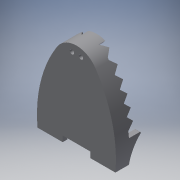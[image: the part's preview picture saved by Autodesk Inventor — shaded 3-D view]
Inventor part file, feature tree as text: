
AUTODESK INVENTOR PART (.ipt)
format: ipt  version: 2016 (Build 200138000, 138)  size: 520,192 bytes
history: native  units: in
note: dims shown in document units (in); Inventor stores cm internally (conversion verified against a paired STEP export)
features: sketch x27, extrude x26, other x12, plane x12, projected_geometry x8, reference x2, fillet x1
ambient origin geometry x8: Origin, YZ Plane, XZ Plane, XY Plane, X Axis, Y Axis, Z Axis, Center Point
bodies: Solid1 (feature_tree)
feature tree (88):
  extrude  "Extrusion1"  Depth=1.0in
  extrude  "Extrusion2"  Depth=0.3937in TaperAngle=0.0deg
  extrude  "Extrusion3"  Depth=1.0in
  extrude  "Extrusion4"  Depth=1.0in TaperAngle=0.0deg
  sketch  "Sketch5"  dims[d12=1.0in d13=0.0in d15=0.5in]
  other  "Work Point1"
  other  "Work Point2"
  other  "Work Point3"
  other  "Work Point4"
  other  "Work Point5"
  other  "Work Point6"
  other  "Work Point7"
  other  "Work Point8"
  other  "Work Point9"
  other  "Work Point10"
  other  "Work Point11"
  other  "Work Point12"
  plane  "Work Plane1"
  plane  "Work Plane2"
  plane  "Work Plane3"
  plane  "Work Plane4"
  plane  "Work Plane5"
  plane  "Work Plane6"
  sketch  "Sketch6"  dims[d16=2.3622in d18=0.45in d19=0.3937in d21=1.0in d23=0.25in]
  sketch  "Sketch7"  dims[d24=0.5in d25=0.25in]
  sketch  "Sketch8"  dims[d26=0.25in d27=0.5in d28=0.25in d29=0.25in d30=0.5in d31=0.25in]
  sketch  "Sketch9"  dims[d32=0.25in d33=0.5in d34=0.25in d35=0.25in d36=0.5in d37=0.25in]
  sketch  "Sketch10"  dims[d38=0.25in d39=0.5in d40=0.25in d44=1.0in d45=0.0in]
  sketch  "Sketch11"  dims[d46=1.0in d47=0.0in d48=1.0in d49=0.0in]
  extrude  "Extrusion5"  Depth=0.5in
  extrude  "Extrusion6"  Depth=0.3937in
  extrude  "Extrusion7"  Depth=0.25in
  extrude  "Extrusion8"  Depth=0.25in
  extrude  "Extrusion9"  Depth=0.25in
  extrude  "Extrusion10"  Depth=1.0in TaperAngle=0.0deg
  plane  "Work Plane7"
  plane  "Work Plane8"
  plane  "Work Plane9"
  plane  "Work Plane10"
  plane  "Work Plane11"
  plane  "Work Plane12"
  sketch  "Sketch13"  dims[d50=1.0in d51=0.0in d52=1.0in d53=0.0in]
  sketch  "Sketch14"  dims[d54=1.0in d55=0.0in d56=0.25in]
  sketch  "Sketch15"  dims[d57=0.5in d58=0.25in]
  sketch  "Sketch16"  dims[d59=0.25in d60=0.5in d61=0.25in d62=0.25in d63=0.5in d64=0.25in]
  sketch  "Sketch17"  dims[d65=0.25in d66=0.5in d67=0.25in d68=0.25in d69=0.5in d70=0.25in]
  sketch  "Sketch18"  dims[d71=0.25in d72=0.5in d73=0.25in d74=1.0in d75=0.0in]
  extrude  "Extrusion11"  Depth=1.0in TaperAngle=0.0deg
  extrude  "Extrusion12"  Depth=1.0in TaperAngle=0.0deg
  extrude  "Extrusion13"  Depth=0.25in
  extrude  "Extrusion14"  Depth=0.25in
  extrude  "Extrusion15"  Depth=0.25in
  extrude  "Extrusion16"  Depth=0.25in
  extrude  "Extrusion17"  Depth=1.0in TaperAngle=0.0deg
  extrude  "Extrusion18"  Depth=1.0in TaperAngle=0.0deg
  extrude  "Extrusion19"  Depth=1.0in TaperAngle=0.0deg
  extrude  "Extrusion20"  Depth=1.0in TaperAngle=0.0deg
  extrude  "Extrusion21"  Depth=32534.0in TaperAngle=0.0deg
  extrude  "Extrusion22"  Depth=4.0in TaperAngle=0.0deg
  extrude  "Extrusion23"  Depth=0.6in
  extrude  "Extrusion24"  Depth=0.25in
  extrude  "Extrusion25"  Depth=1.0in TaperAngle=0.0deg
  fillet  "Fillet1"  Radius=0.2953in
  extrude  "Extrusion26"  Depth=0.1969in
  sketch  "Sketch1"  dims[d0=4.5in d1=1.0in]
  reference  "Reference1"
  sketch  "Sketch2"  dims[d2=0.1969in d3=0.0in d4=0.3937in d5=0.0in]
  projected_geometry  "Projected Loop1"
  sketch  "Sketch3"  dims[d6=0.9843in d7=1.0in]
  sketch  "Sketch4"  dims[d8=4.0in d9=0.0in d10=1.0in d11=0.0in]
  projected_geometry  "Projected Loop2"
  projected_geometry  "Projected Loop3"
  sketch  "Sketch19"  dims[d76=1.0in d77=0.0in d78=1.0in d79=0.0in]
  projected_geometry  "Projected Loop4"
  sketch  "Sketch20"  dims[d80=1.0in d81=0.0in d82=1.0in d83=0.0in]
  reference  "Reference2"
  sketch  "Sketch21"  dims[d84=1.0in d85=0.0in d86=1.0in d87=0.0in]
  sketch  "Sketch22"  dims[d88=4.0in d89=0.0in d90=32534.0in d91=0.0in]
  sketch  "Sketch23"  dims[d92=4.0in d93=1.0in d94=0.0in d95=0.0in d96=4.0in d97=0.0in]
  projected_geometry  "Projected Loop5"
  sketch  "Sketch24"  dims[d98=4.0in d99=0.0in d100=0.6in]
  projected_geometry  "Projected Loop6"
  sketch  "Sketch25"  dims[d101=1.2in d102=0.25in]
  sketch  "Sketch26"  dims[d103=4.0in d104=0.0in d105=1.0in d106=0.0in d107=0.2953in d108=0.0in]
  projected_geometry  "Projected Loop7"
  sketch  "Sketch27"  dims[d109=0.0394in d110=0.1969in]
  projected_geometry  "Projected Loop8"
  sketch  "Sketch28"  dims[d111=0.1969in d112=0.3937in d113=0.19in d114=0.19in d115=1.0in d116=0.0in]
